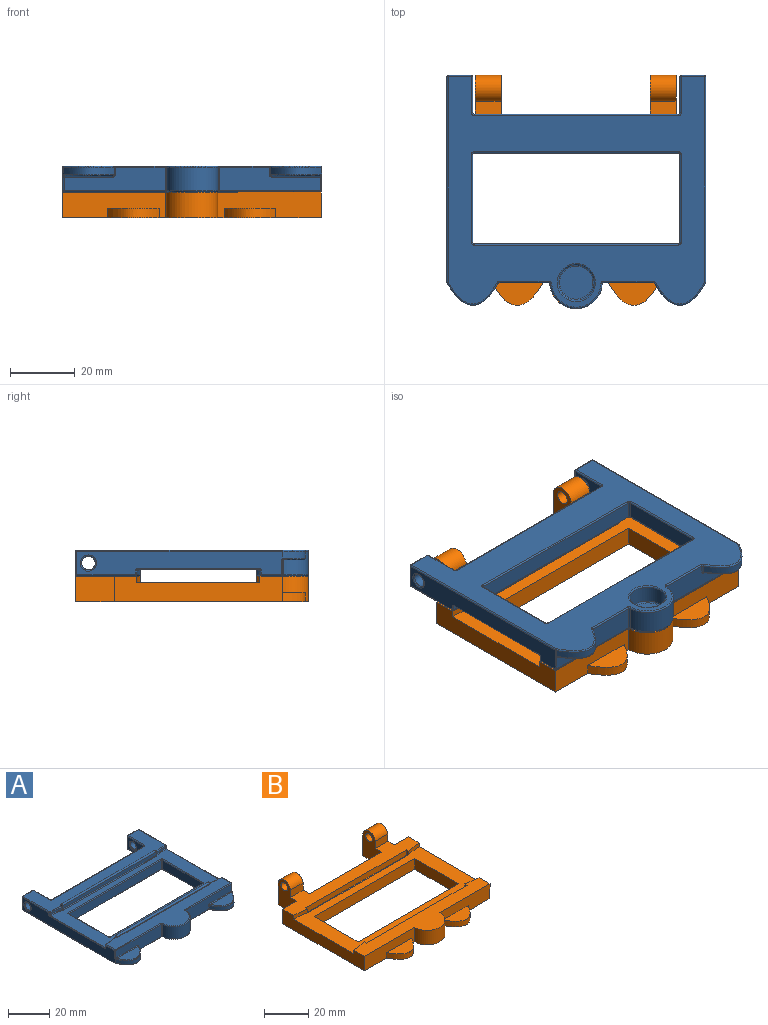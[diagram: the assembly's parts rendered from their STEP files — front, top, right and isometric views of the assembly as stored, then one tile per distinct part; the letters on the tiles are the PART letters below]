
ASSEMBLY  parts=2 mates=1
PART A: 178 faces, bbox 83x72.7x9 mm
  f0: torus R=0.8mm, axis (0,0,1), area 0.1mm2, adj f15,f30,f94,f109,f110
  f1: plane 79.2x15.19mm, normal (0,0,1), area 606.1mm2, adj f3,f7,f93,f108,f115,f120,f125,f130
  f2: torus R=0.8mm, axis (0,0,1), area 0.1mm2, adj f4,f15,f30,f78,f94,f171
  f3: bspline ~9.62x1.75mm, area 4.8mm2, adj f1,f5,f23,f86,f171
  f4: cylinder r=0.4mm len=1.2mm, axis (0,0,-1), area 0.1mm2, adj f2,f5,f23,f171
  f5: sphere r=0.4mm, area 0mm2, adj f3,f4,f171
  f6: sphere r=0.4mm, area 0mm2, adj f7,f109,f170
  f7: bspline ~10.42x1.6mm, area 4.8mm2, adj f1,f6,f24,f126,f170
  f8: plane 79.2x19.19mm, normal (0,0,1), area 682.2mm2, adj f9,f14,f45,f46,f52,f57,f62,f71
  f9: bspline ~10.42x1.6mm, area 4.8mm2, adj f8,f10,f22,f48,f167
  f10: sphere r=0.4mm, area 0mm2, adj f9,f11,f167
  f11: cylinder r=0.4mm len=1.2mm, axis (0,0,-1), area 0.1mm2, adj f10,f12,f22,f167
  f12: torus R=0.8mm, axis (0,0,1), area 0.1mm2, adj f11,f15,f31,f61,f79,f167
  f13: sphere r=0.4mm, area 0mm2, adj f14,f80,f168
  f14: bspline ~9.62x1.75mm, area 4.8mm2, adj f8,f13,f25,f88,f168
  f15: plane 79.2x37.2mm, normal (0,0,1), area 941.7mm2, adj f0,f2,f12,f60,f61,f78,f79,f87
  f16: plane 31.21x7.2mm, normal (0,-1,0), area 177.4mm2, adj f67,f74,f75,f91,f92,f107,f108
  f17: plane 31.21x7.2mm, normal (0,-1,0), area 177.4mm2, adj f118,f119,f129,f130,f134,f137,f138
  f18: plane 63.2x7.2mm, normal (0,1,0), area 455mm2, adj f62,f63,f82,f83
  f19: plane 63.49x7.2mm, normal (1,0,0), area 358.8mm2, adj f96,f97,f103,f111,f112,f116,f121,f122
  f20: plane 79.21x71.2mm, normal (0,0,-1), area 2494.5mm2, adj f54,f59,f64,f72,f73,f83,f84,f90
  f21: plane 63.49x7.2mm, normal (-1,0,0), area 358.8mm2, adj f45,f50,f51,f56,f59,f60,f69,f70
  f22: extruded ~7.56x1.2mm, area 9.2mm2, adj f9,f11,f51,f61
  f23: extruded ~7.56x1.2mm, area 9.2mm2, adj f3,f4,f77,f78
  f24: extruded ~7.56x1.2mm, area 9.2mm2, adj f7,f109,f110,f121
  f25: extruded ~7.56x1.2mm, area 9.2mm2, adj f14,f80,f95,f96
  f26: plane 63.2x5.2mm, normal (0,-1,0), area 328.6mm2, adj f151,f160,f161,f165
  f27: plane 27.2x5.2mm, normal (1,0,0), area 141.4mm2, adj f152,f153,f161,f162
  f28: plane 63.2x5.2mm, normal (0,1,0), area 328.6mm2, adj f146,f149,f153,f154
  f29: plane 27.2x5.2mm, normal (-1,0,0), area 141.4mm2, adj f149,f150,f159,f160
  f30: plane 64.01x2.05mm, normal (0,1,0), area 128mm2, adj f0,f2,f94,f109,f170,f171,f173
  f31: plane 64.01x2.05mm, normal (0,-1,0), area 127.9mm2, adj f12,f79,f80,f167,f168,f176
  f32: plane 11.2x7.2mm, normal (-1,0,0), area 61mm2, adj f81,f82,f99,f100,f143
  f33: plane 7.2x7.2mm, normal (0,1,0), area 51.8mm2, adj f98,f99,f112,f113
  f34: plane 11.2x7.2mm, normal (1,0,0), area 61mm2, adj f52,f53,f63,f64,f144
  f35: plane 7.2x7.2mm, normal (0,1,0), area 51.8mm2, adj f46,f50,f53,f54
  f36: cylinder r=2.1mm len=7.2mm, axis (-1,0,0), area 95mm2, adj f144,f145
  f37: cylinder r=2.1mm len=7.2mm, axis (-1,0,0), area 95mm2, adj f142,f143
  f38: cylinder r=8mm len=15.98mm, axis (0,0,-1), area 175.5mm2, adj f106,f107,f119,f120
  f39: cylinder r=5.5mm len=11mm, axis (0,0,-1), area 179.7mm2, adj f140,f141
  f40: plane 10.2x10.2mm, normal (0,0,-1), area 81.7mm2, adj f141
  f41: extruded ~15.83x6.91mm, area 48.1mm2, adj f65,f68,f69,f73,f74
  f42: plane 14.62x6.2mm, normal (0,0,1), area 60.1mm2, adj f65,f75
  f43: extruded ~15.83x6.91mm, area 48.1mm2, adj f123,f128,f129,f132,f133
  f44: plane 14.62x6.2mm, normal (0,0,1), area 60.1mm2, adj f128,f137
  f45: cylinder r=0.4mm len=18.2mm, axis (0,-1,0), area 11.4mm2, adj f8,f21,f47,f48
  f46: cylinder r=0.4mm len=7.2mm, axis (1,0,0), area 4.5mm2, adj f8,f35,f47,f49
  f47: sphere r=0.4mm, area 0.3mm2, adj f45,f46,f50
  f48: sphere r=0.4mm, area 0.2mm2, adj f9,f45,f51
  f49: sphere r=0.4mm, area 0.2mm2, adj f46,f52,f53
  f50: cylinder r=0.4mm len=7.2mm, axis (0,0,1), area 4.5mm2, adj f21,f35,f47,f55
  f51: cylinder r=0.4mm len=1.2mm, axis (0,0,-1), area 0.7mm2, adj f21,f22,f48,f56
  f52: cylinder r=0.4mm len=11.2mm, axis (0,-1,0), area 7mm2, adj f8,f34,f49,f57
  f53: cylinder r=0.4mm len=7.2mm, axis (0,0,1), area 4.5mm2, adj f34,f35,f49,f58
  f54: cylinder r=0.4mm len=7.2mm, axis (1,0,0), area 4.5mm2, adj f20,f35,f55,f58
  f55: sphere r=0.4mm, area 0.2mm2, adj f50,f54,f59
  f56: bspline ~0.98x0.94mm, area 0.5mm2, adj f21,f51,f60,f61
  f57: torus R=0.8mm, axis (0,0,1), area 0.5mm2, adj f8,f52,f62,f63
  f58: sphere r=0.4mm, area 0.3mm2, adj f53,f54,f64
  f59: cylinder r=0.4mm len=63.49mm, axis (0,1,0), area 39.9mm2, adj f20,f21,f55,f66
  f60: cylinder r=0.4mm len=37.2mm, axis (0,-1,0), area 23.4mm2, adj f15,f21,f56,f70
  f61: bspline ~9.72x1.76mm, area 4.8mm2, adj f12,f15,f22,f56
  f62: cylinder r=0.4mm len=63.2mm, axis (-1,0,0), area 39.7mm2, adj f8,f18,f57,f71
  f63: cylinder r=0.4mm len=7.2mm, axis (0,0,-1), area 4.5mm2, adj f18,f34,f57,f72
  f64: cylinder r=0.4mm len=11.2mm, axis (0,-1,0), area 7mm2, adj f20,f34,f58,f72
  f65: bspline ~15.87x7.16mm, area 13mm2, adj f41,f42,f67,f68
  f66: sphere r=0.4mm, area 0.1mm2, adj f59,f69,f73
  f67: bspline ~1.2x0.9mm, area 0.5mm2, adj f16,f65,f74,f75
  f68: bspline ~0.84x0.84mm, area 0.3mm2, adj f41,f65,f75,f76
  f69: cylinder r=0.4mm len=2.38mm, axis (0,0,-1), area 0.5mm2, adj f21,f41,f66,f76
  f70: bspline ~0.98x0.94mm, area 0.5mm2, adj f21,f60,f77,f78
  f71: torus R=0.8mm, axis (0,0,1), area 0.5mm2, adj f8,f62,f81,f82
  f72: torus R=0.8mm, axis (0,0,-1), area 0.5mm2, adj f20,f63,f64,f83
  f73: bspline ~16.17x7.39mm, area 13.5mm2, adj f20,f41,f66,f84
  f74: cylinder r=0.4mm len=2.2mm, axis (0,0,-1), area 0.9mm2, adj f16,f41,f67,f84
  f75: cylinder r=0.4mm len=14.9mm, axis (-1,0,0), area 9.3mm2, adj f16,f42,f67,f68,f85
  f76: sphere r=0.4mm, area 0.1mm2, adj f68,f69,f85
  f77: cylinder r=0.4mm len=1.2mm, axis (0,0,-1), area 0.7mm2, adj f21,f23,f70,f86
  f78: bspline ~9.72x1.76mm, area 4.8mm2, adj f2,f15,f23,f70
  f79: cylinder r=0.4mm len=63.9mm, axis (1,0,0), area 40.2mm2, adj f12,f15,f31,f87
  f80: cylinder r=0.4mm len=1.2mm, axis (0,0,-1), area 0.1mm2, adj f13,f25,f31,f87
  f81: cylinder r=0.4mm len=11.2mm, axis (0,1,0), area 7mm2, adj f8,f32,f71,f89
  f82: cylinder r=0.4mm len=7.2mm, axis (0,0,1), area 4.5mm2, adj f18,f32,f71,f90
  f83: cylinder r=0.4mm len=63.2mm, axis (-1,0,0), area 39.7mm2, adj f18,f20,f72,f90
  f84: torus R=0.8mm, axis (0,0,-1), area 0.4mm2, adj f20,f73,f74,f91
  f85: torus R=0.8mm, axis (1,0,0), area 0.3mm2, adj f21,f75,f76,f92
  f86: sphere r=0.4mm, area 0.3mm2, adj f3,f77,f93
  f87: torus R=0.8mm, axis (0,0,1), area 0.1mm2, adj f15,f79,f80,f95
  f88: sphere r=0.4mm, area 0.3mm2, adj f14,f96,f97
  f89: sphere r=0.4mm, area 0.3mm2, adj f81,f98,f99
  f90: torus R=0.8mm, axis (0,0,-1), area 0.5mm2, adj f20,f82,f83,f100
  f91: cylinder r=0.4mm len=15.38mm, axis (-1,0,0), area 9.7mm2, adj f16,f20,f84,f101
  f92: cylinder r=0.4mm len=4.2mm, axis (0,0,-1), area 2.6mm2, adj f16,f21,f85,f102
  f93: cylinder r=0.4mm len=6.2mm, axis (0,-1,0), area 3.9mm2, adj f1,f21,f86,f102
  f94: cylinder r=0.4mm len=63.9mm, axis (-1,0,0), area 40.2mm2, adj f0,f2,f15,f30
  f95: bspline ~9.72x1.76mm, area 4.8mm2, adj f15,f25,f87,f103
  f96: cylinder r=0.4mm len=1.2mm, axis (0,0,-1), area 0.7mm2, adj f19,f25,f88,f103
  f97: cylinder r=0.4mm len=18.2mm, axis (0,1,0), area 11.4mm2, adj f8,f19,f88,f104
  f98: cylinder r=0.4mm len=7.2mm, axis (1,0,0), area 4.5mm2, adj f8,f33,f89,f104
  f99: cylinder r=0.4mm len=7.2mm, axis (0,0,1), area 4.5mm2, adj f32,f33,f89,f105
  f100: cylinder r=0.4mm len=11.2mm, axis (0,1,0), area 7mm2, adj f20,f32,f90,f105
  f101: torus R=0.8mm, axis (0,0,-1), area 0.5mm2, adj f20,f91,f106,f107
  f102: sphere r=0.4mm, area 0.2mm2, adj f92,f93,f108
  f103: bspline ~0.98x0.94mm, area 0.5mm2, adj f19,f95,f96,f111
  f104: sphere r=0.4mm, area 0.2mm2, adj f97,f98,f112
  f105: sphere r=0.4mm, area 0.3mm2, adj f99,f100,f113
  f106: torus R=7.6mm, axis (0,0,-1), area 15mm2, adj f20,f38,f101,f114
  f107: cylinder r=0.4mm len=7.2mm, axis (0,0,-1), area 4.4mm2, adj f16,f38,f101,f115
  f108: cylinder r=0.4mm len=31.21mm, axis (-1,0,0), area 19.6mm2, adj f1,f16,f102,f115
  f109: cylinder r=0.4mm len=1.2mm, axis (0,0,-1), area 0.1mm2, adj f0,f6,f24,f30
  f110: bspline ~9.72x1.76mm, area 4.8mm2, adj f0,f15,f24,f116
  f111: cylinder r=0.4mm len=37.2mm, axis (0,1,0), area 23.4mm2, adj f15,f19,f103,f116
  f112: cylinder r=0.4mm len=7.2mm, axis (0,0,1), area 4.5mm2, adj f19,f33,f104,f117
  f113: cylinder r=0.4mm len=7.2mm, axis (1,0,0), area 4.5mm2, adj f20,f33,f105,f117
  f114: torus R=0.8mm, axis (0,0,-1), area 0.5mm2, adj f20,f106,f118,f119
  f115: torus R=0.8mm, axis (0,0,1), area 0.5mm2, adj f1,f107,f108,f120
  f116: bspline ~0.98x0.94mm, area 0.5mm2, adj f19,f110,f111,f121
  f117: sphere r=0.4mm, area 0.2mm2, adj f112,f113,f122
  f118: cylinder r=0.4mm len=15.38mm, axis (-1,0,0), area 9.7mm2, adj f17,f20,f114,f124
  f119: cylinder r=0.4mm len=7.2mm, axis (0,0,-1), area 4.4mm2, adj f17,f38,f114,f125
  f120: torus R=7.6mm, axis (0,0,1), area 15mm2, adj f1,f38,f115,f125
  f121: cylinder r=0.4mm len=1.2mm, axis (0,0,-1), area 0.7mm2, adj f19,f24,f116,f126
  f122: cylinder r=0.4mm len=63.49mm, axis (0,-1,0), area 39.9mm2, adj f19,f20,f117,f127
  f123: bspline ~16.17x7.39mm, area 13.5mm2, adj f20,f43,f124,f127
  f124: torus R=0.8mm, axis (0,0,-1), area 0.4mm2, adj f20,f118,f123,f129
  f125: torus R=0.8mm, axis (0,0,1), area 0.5mm2, adj f1,f119,f120,f130
  f126: sphere r=0.4mm, area 0.2mm2, adj f7,f121,f131
  f127: sphere r=0.4mm, area 0.1mm2, adj f122,f123,f132
  f128: bspline ~16.19x7.57mm, area 13mm2, adj f43,f44,f133,f134
  f129: cylinder r=0.4mm len=2.2mm, axis (0,0,-1), area 0.9mm2, adj f17,f43,f124,f134
  f130: cylinder r=0.4mm len=31.21mm, axis (-1,0,0), area 19.6mm2, adj f1,f17,f125,f135
  f131: cylinder r=0.4mm len=6.2mm, axis (0,1,0), area 3.9mm2, adj f1,f19,f126,f135
  f132: cylinder r=0.4mm len=2.38mm, axis (0,0,-1), area 0.5mm2, adj f19,f43,f127,f136
  f133: bspline ~0.84x0.84mm, area 0.3mm2, adj f43,f128,f136,f137
  f134: bspline ~1.16x0.96mm, area 0.5mm2, adj f17,f128,f129,f137
  f135: sphere r=0.4mm, area 0.3mm2, adj f130,f131,f138
  f136: sphere r=0.4mm, area 0.1mm2, adj f132,f133,f139
  f137: cylinder r=0.4mm len=14.9mm, axis (-1,0,0), area 9.3mm2, adj f17,f44,f133,f134,f139
  f138: cylinder r=0.4mm len=4.2mm, axis (0,0,1), area 2.6mm2, adj f17,f19,f135,f139
  f139: torus R=0.8mm, axis (1,0,0), area 0.3mm2, adj f19,f136,f137,f138
  f140: torus R=5.9mm, axis (0,0,-1), area 22.3mm2, adj f20,f39
  f141: torus R=5.1mm, axis (0,0,1), area 21.1mm2, adj f39,f40
  f142: torus R=2.5mm, axis (1,0,0), area 8.9mm2, adj f19,f37
  f143: torus R=2.5mm, axis (-1,0,0), area 8.9mm2, adj f32,f37
  f144: torus R=2.5mm, axis (-1,0,0), area 8.9mm2, adj f34,f36
  f145: torus R=2.5mm, axis (1,0,0), area 8.9mm2, adj f21,f36
  f146: cylinder r=0.4mm len=63.2mm, axis (1,0,0), area 39.7mm2, adj f20,f28,f147,f148
  f147: torus R=0.8mm, axis (0,0,-1), area 0.5mm2, adj f20,f146,f149,f150
  f148: torus R=0.8mm, axis (0,0,-1), area 0.5mm2, adj f20,f146,f152,f153
  f149: cylinder r=0.4mm len=5.2mm, axis (0,0,-1), area 3.3mm2, adj f28,f29,f147,f155
  f150: cylinder r=0.4mm len=27.2mm, axis (0,1,0), area 17.1mm2, adj f20,f29,f147,f156
  f151: cylinder r=0.4mm len=63.2mm, axis (-1,0,0), area 39.7mm2, adj f20,f26,f156,f157
  f152: cylinder r=0.4mm len=27.2mm, axis (0,-1,0), area 17.1mm2, adj f20,f27,f148,f157
  f153: cylinder r=0.4mm len=5.2mm, axis (0,0,1), area 3.3mm2, adj f27,f28,f148,f158
  f154: cylinder r=0.4mm len=63.2mm, axis (-1,0,0), area 39.7mm2, adj f15,f28,f155,f158
  f155: torus R=0.8mm, axis (0,0,1), area 0.5mm2, adj f15,f149,f154,f159
  f156: torus R=0.8mm, axis (0,0,-1), area 0.5mm2, adj f20,f150,f151,f160
  f157: torus R=0.8mm, axis (0,0,-1), area 0.5mm2, adj f20,f151,f152,f161
  f158: torus R=0.8mm, axis (0,0,1), area 0.5mm2, adj f15,f153,f154,f162
  f159: cylinder r=0.4mm len=27.2mm, axis (0,-1,0), area 17.1mm2, adj f15,f29,f155,f163
  f160: cylinder r=0.4mm len=5.2mm, axis (0,0,1), area 3.3mm2, adj f26,f29,f156,f163
  f161: cylinder r=0.4mm len=5.2mm, axis (0,0,-1), area 3.3mm2, adj f26,f27,f157,f164
  f162: cylinder r=0.4mm len=27.2mm, axis (0,1,0), area 17.1mm2, adj f15,f27,f158,f164
  f163: torus R=0.8mm, axis (0,0,1), area 0.5mm2, adj f15,f159,f160,f165
  f164: torus R=0.8mm, axis (0,0,1), area 0.5mm2, adj f15,f161,f162,f165
  f165: cylinder r=0.4mm len=63.2mm, axis (1,0,0), area 39.7mm2, adj f15,f26,f163,f164
  f166: plane 64x0.4mm, normal (0,1,0), area 25.6mm2, adj f8,f167,f168,f176
  f167: plane 2.08x1.23mm, normal (-1,0,0), area 0.5mm2, adj f8,f9,f10,f11,f12,f31,f166,f177
  f168: plane 1.23x0.83mm, normal (1,0,0), area 0.5mm2, adj f8,f13,f14,f31,f166,f175
  f169: plane 64x0.4mm, normal (0,-1,0), area 25.6mm2, adj f1,f170,f171,f173
  f170: plane 1.23x0.83mm, normal (1,0,0), area 0.5mm2, adj f1,f6,f7,f30,f169,f172
  f171: plane 2.08x1.23mm, normal (-1,0,0), area 0.5mm2, adj f1,f2,f3,f4,f5,f30,f169,f174
  f172: cylinder r=0.6mm len=1.2mm, axis (0,-1,0), area 0.6mm2, adj f170,f173
  f173: cylinder r=0.6mm len=64mm, axis (-1,0,0), area 119.5mm2, adj f30,f169,f172,f174
  f174: cylinder r=0.6mm len=1.2mm, axis (0,1,0), area 0.6mm2, adj f171,f173
  f175: cylinder r=0.6mm len=1.2mm, axis (0,-1,0), area 0.6mm2, adj f168,f176
  f176: cylinder r=0.6mm len=64mm, axis (1,0,0), area 119.5mm2, adj f31,f166,f175,f177
  f177: cylinder r=0.6mm len=1.2mm, axis (0,1,0), area 0.6mm2, adj f167,f176
PART B: 48 faces, bbox 80x73.6x15.5 mm
  f0: plane 80x12mm, normal (0,0,1), area 603.7mm2, adj f3,f4,f5,f8,f10,f11,f14,f19
  f1: plane 80x16mm, normal (0,0,1), area 640.3mm2, adj f2,f5,f6,f10,f12,f13,f29,f39
  f2: plane 32x8mm, normal (0,-1,0), area 208mm2, adj f1,f5,f7,f29,f34,f35
  f3: plane 9x8mm, normal (0,1,0), area 72mm2, adj f0,f7,f10,f22
  f4: plane 46x8mm, normal (0,1,0), area 368mm2, adj f0,f7,f19,f23
  f5: plane 52x8mm, normal (1,0,0), area 340mm2, adj f0,f1,f2,f7,f8,f9,f13,f14
  f6: plane 32x8mm, normal (0,-1,0), area 208mm2, adj f1,f7,f10,f29,f36,f37
  f7: plane 80x73.63mm, normal (0,0,-1), area 2714.8mm2, adj f2,f3,f4,f5,f6,f8,f10,f15
  f8: plane 9x8mm, normal (0,1,0), area 72mm2, adj f0,f5,f7,f20
  f9: plane 80x38mm, normal (0,0,1), area 1109.3mm2, adj f5,f10,f11,f12,f13,f14,f15,f16
  f10: plane 52x8mm, normal (-1,0,0), area 340mm2, adj f0,f1,f3,f6,f7,f9,f11,f12
  f11: extruded ~8x2mm, area 16.2mm2, adj f0,f9,f10,f45
  f12: extruded ~8x2mm, area 16.2mm2, adj f1,f9,f10,f41
  f13: extruded ~8x2mm, area 16.2mm2, adj f1,f5,f9,f40
  f14: extruded ~8x2mm, area 16.2mm2, adj f0,f5,f9,f46
  f15: plane 64x6mm, normal (0,-1,0), area 384mm2, adj f7,f9,f16,f18
  f16: plane 28x6mm, normal (1,0,0), area 168mm2, adj f7,f9,f15,f17
  f17: plane 64x6mm, normal (0,1,0), area 384mm2, adj f7,f9,f16,f18
  f18: plane 28x6mm, normal (-1,0,0), area 168mm2, adj f7,f9,f15,f17
  f19: plane 15.5x12mm, normal (-1,0,0), area 135.4mm2, adj f0,f4,f7,f21,f27,f28,f33
  f20: plane 15.5x12mm, normal (1,0,0), area 135.4mm2, adj f0,f7,f8,f21,f27,f28,f33
  f21: plane 12x8mm, normal (0,1,0), area 96mm2, adj f7,f19,f20,f27
  f22: plane 15.5x12mm, normal (-1,0,0), area 135.4mm2, adj f0,f3,f7,f24,f25,f26,f32
  f23: plane 15.5x12mm, normal (1,0,0), area 135.4mm2, adj f0,f4,f7,f24,f25,f26,f32
  f24: plane 12x8mm, normal (0,1,0), area 96mm2, adj f7,f22,f23,f25
  f25: cylinder r=4.04mm len=8mm, axis (-1,0,0), area 92.8mm2, adj f22,f23,f24,f26
  f26: plane 8x4mm, normal (0,-1,0), area 32mm2, adj f0,f22,f23,f25
  f27: cylinder r=4.04mm len=8mm, axis (-1,0,0), area 92.8mm2, adj f19,f20,f21,f28
  f28: plane 8x4mm, normal (0,-1,0), area 32mm2, adj f0,f19,f20,f27
  f29: cylinder r=8mm len=16mm, axis (0,0,-1), area 201.1mm2, adj f1,f2,f6,f7
  f30: cylinder r=5.5mm len=11mm, axis (0,0,-1), area 207.3mm2, adj f7,f31
  f31: plane 11x11mm, normal (0,0,-1), area 95mm2, adj f30
  f32: cylinder r=2.1mm len=8mm, axis (-1,0,0), area 105.6mm2, adj f22,f23
  f33: cylinder r=2.1mm len=8mm, axis (-1,0,0), area 105.6mm2, adj f19,f20
  f34: extruded ~16x7mm, area 66.6mm2, adj f2,f7,f35
  f35: plane 16x9.63mm, normal (0,0,1), area 74.7mm2, adj f2,f34
  f36: extruded ~16x7mm, area 66.6mm2, adj f6,f7,f37
  f37: plane 16x9.63mm, normal (0,0,1), area 74.7mm2, adj f6,f36
  f38: plane 64x1mm, normal (0,-1,0), area 64mm2, adj f9,f40,f41,f42
  f39: plane 64x3mm, normal (0,1,0), area 192mm2, adj f1,f40,f41,f42
  f40: plane 3x1.4mm, normal (-1,0,0), area 4.2mm2, adj f1,f13,f38,f39,f42
  f41: plane 3x1.4mm, normal (1,0,0), area 4.2mm2, adj f1,f12,f38,f39,f42
  f42: plane 64x1.4mm, normal (0,0,1), area 89.6mm2, adj f38,f39,f40,f41
  f43: plane 64x1mm, normal (0,1,0), area 64mm2, adj f9,f45,f46,f47
  f44: plane 64x3mm, normal (0,-1,0), area 192mm2, adj f0,f45,f46,f47
  f45: plane 3x1.4mm, normal (1,0,0), area 4.2mm2, adj f0,f11,f43,f44,f47
  f46: plane 3x1.4mm, normal (-1,0,0), area 4.2mm2, adj f0,f14,f43,f44,f47
  f47: plane 64x1.4mm, normal (0,0,1), area 89.6mm2, adj f43,f44,f45,f46
PLACE A rot(axis=(0,1,0),180deg) t=(71.44,-6.58,14.65)mm
PLACE B rot(axis=(0.35,-0.78,-0.52),0deg) t=(-8.76,-6.58,-1.35)mm
MATE revolute B.f32 <-> A.f36  axis (-1,0,0) through (31.24,53.42,10.65)mm
